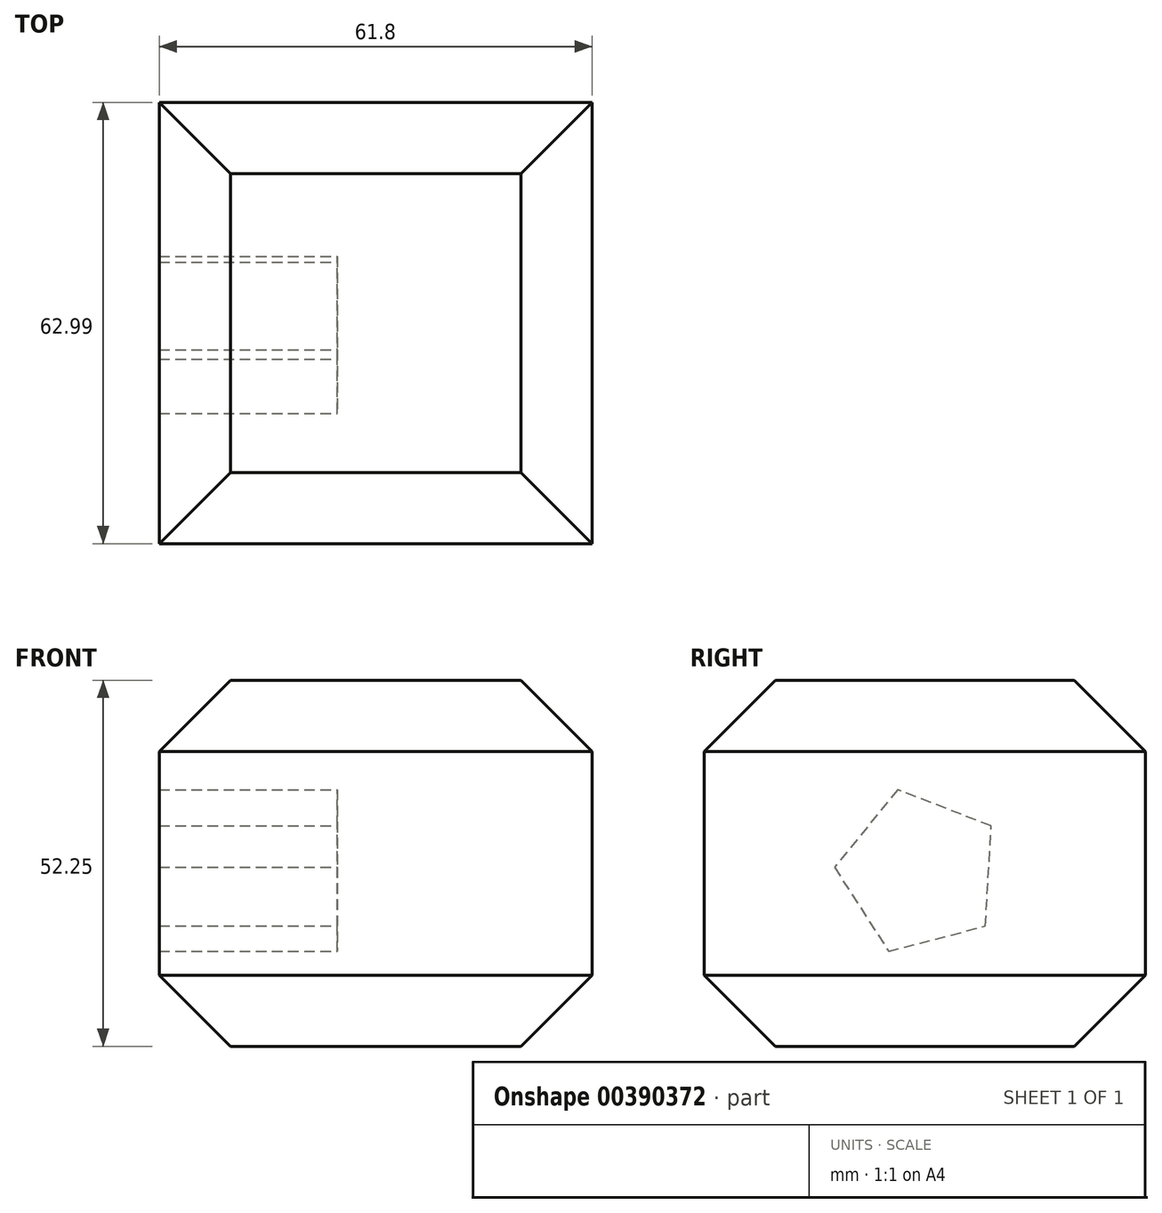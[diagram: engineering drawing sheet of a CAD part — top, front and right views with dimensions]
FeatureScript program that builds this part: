
annotation { "Feature Type Name" : "Feature", "Feature Type Description" : "" }
export const myFeature = defineFeature(function(context is Context, id is Id, definition is map)
    precondition{}
    {
        {
            var Q0;
            Q0=qCreatedBy(makeId("Front.planeOp"),FACE);
            var sketch = newSketch(context, id + "F0", { "sketchPlane" : qUnion([Q0])});
            skLineSegment(sketch, "E0.bottom", {"start": v(0, 0) * mm, "end": v(61.8, 0) * mm});
            skLineSegment(sketch, "E0.top", {"start": v(0, 52.25) * mm, "end": v(61.8, 52.25) * mm});
            skLineSegment(sketch, "E0.left", {"start": v(0, 0) * mm, "end": v(0, 52.25) * mm});
            skLineSegment(sketch, "E0.right", {"start": v(61.8, 0) * mm, "end": v(61.8, 52.25) * mm});
            skSolve(sketch);
        }
        {
            var Q0;
            Q0=makeQuery(id+"F0.imprint","IMPRINT",FACE,{"disambiguationData":[TD([[makeQuery(id+"F0.imprint","IMPRINT",EDGE,{"derivedFrom":sQuery(id+"F0.wireOp",EDGE,"E0.bottom")}),1.0]])]});
            extrude(context, id + "F1", {"entities" : qUnion([Q0]), "depth" : 63 * mm});
        }
        {
            var Q0;
            Q0=makeQuery(id+"F1.opExtrude","SWEPT_EDGE",EDGE,{"disambiguationData":[OSD([sQuery(id+"F0.wireOp",EDGE,"E0.top"),sQuery(id+"F0.wireOp",EDGE,"E0.right")])]});
            var Q1;
            Q1=makeQuery(id+"F1.opExtrude","CAP_EDGE",EDGE,{"disambiguationData":[OSD([sQuery(id+"F0.wireOp",EDGE,"E0.top")])],"isStart":false});
            var Q2;
            Q2=makeQuery(id+"F1.opExtrude","CAP_EDGE",EDGE,{"disambiguationData":[OSD([sQuery(id+"F0.wireOp",EDGE,"E0.top")])],"isStart":true});
            var Q3;
            Q3=makeQuery(id+"F1.opExtrude","SWEPT_EDGE",EDGE,{"disambiguationData":[OSD([sQuery(id+"F0.wireOp",EDGE,"E0.top"),sQuery(id+"F0.wireOp",EDGE,"E0.left")])]});
            var Q4;
            Q4=makeQuery(id+"F1.opExtrude","SWEPT_EDGE",EDGE,{"disambiguationData":[OSD([sQuery(id+"F0.wireOp",EDGE,"E0.bottom"),sQuery(id+"F0.wireOp",EDGE,"E0.right")])]});
            var Q5;
            Q5=makeQuery(id+"F1.opExtrude","CAP_EDGE",EDGE,{"disambiguationData":[OSD([sQuery(id+"F0.wireOp",EDGE,"E0.bottom")])],"isStart":false});
            var Q6;
            Q6=makeQuery(id+"F1.opExtrude","SWEPT_FACE",FACE,{"disambiguationData":[OSD([sQuery(id+"F0.wireOp",EDGE,"E0.bottom")])]});
            chamfer(context, id + "F2", {"entities" : qUnion([Q0, Q1, Q2, Q3, Q4, Q5, Q6]), "width" : 10.16 * mm, "tangentPropagation" : true});
        }
        {
            var Q0;
            Q0=makeQuery(id+"F1.opExtrude","SWEPT_FACE",FACE,{"disambiguationData":[OSD([sQuery(id+"F0.wireOp",EDGE,"E0.left")])]});
            var sketch = newSketch(context, id + "F3", { "sketchPlane" : qUnion([Q0])});
            skCircle(sketch, "E1.cCircle", {"center": v(32.25, 24.87) * mm, "radius": 9.84 * mm, "construction": true});
            skLineSegment(sketch, "E1.0", {"start": v(35.34, 36.63) * mm, "end": v(44.39, 25.56) * mm});
            skLineSegment(sketch, "E1.1", {"start": v(44.39, 25.56) * mm, "end": v(36.65, 13.54) * mm});
            skLineSegment(sketch, "E1.2", {"start": v(36.65, 13.54) * mm, "end": v(22.83, 17.17) * mm});
            skLineSegment(sketch, "E1.3", {"start": v(22.83, 17.17) * mm, "end": v(22.02, 31.45) * mm});
            skLineSegment(sketch, "E1.4", {"start": v(22.02, 31.45) * mm, "end": v(35.34, 36.63) * mm});
            skPoint(sketch, "E1.0.midPoint", {"position": v(39.86, 31.1) * mm});
            skSolve(sketch);
        }
        {
            var Q0;
            Q0=makeQuery(id+"F3.imprint","IMPRINT",FACE,{"disambiguationData":[TD([[makeQuery(id+"F3.imprint","IMPRINT",EDGE,{"derivedFrom":sQuery(id+"F3.wireOp",EDGE,"E1.0")}),-1.0]])]});
            extrude(context, id + "F4", {"entities" : qUnion([Q0]), "operationType" : NewBodyOperationType.REMOVE, "oppositeDirection" : true, "depth" : 25.4 * mm});
        }
        {
            var Q0;
            Q0=makeQuery(id+"F4.boolean.opBoolean","COPY",FACE,{"derivedFrom":makeQuery(id+"F4.opExtrude","CAP_FACE",FACE,{"disambiguationData":[OSD([sQuery(id+"F3.wireOp",EDGE,"E1.0"),sQuery(id+"F3.wireOp",EDGE,"E1.1"),sQuery(id+"F3.wireOp",EDGE,"E1.2"),sQuery(id+"F3.wireOp",EDGE,"E1.3"),sQuery(id+"F3.wireOp",EDGE,"E1.4")])],"isStart":false})});
            extrude(context, id + "F5", {"entities" : qUnion([Q0]), "depth" : 25.4 * mm});
        }
    });
